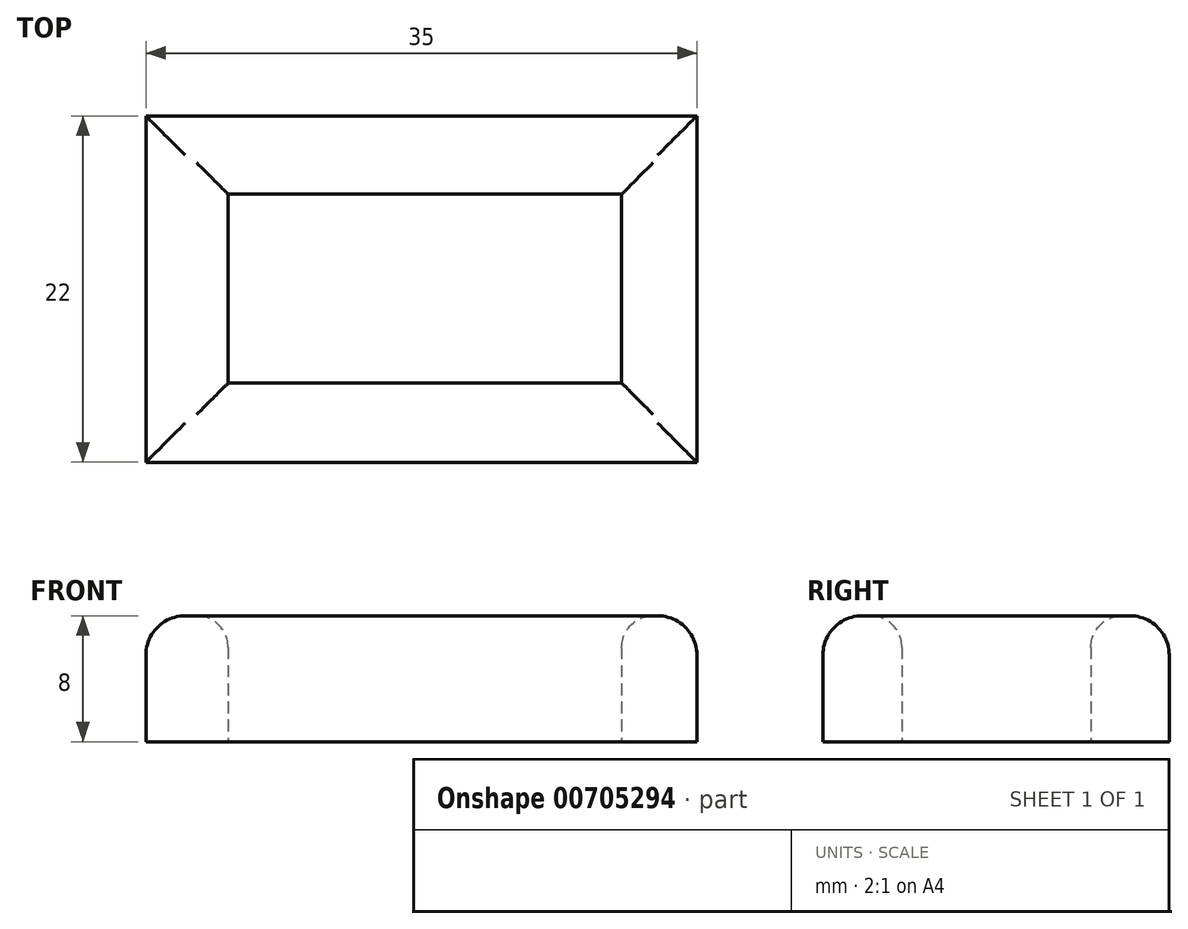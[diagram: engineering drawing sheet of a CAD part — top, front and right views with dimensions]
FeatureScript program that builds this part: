
annotation { "Feature Type Name" : "Feature", "Feature Type Description" : "" }
export const myFeature = defineFeature(function(context is Context, id is Id, definition is map)
    precondition{}
    {
        {
            var Q0;
            Q0=qCreatedBy(makeId("Top.planeOp"),FACE);
            var sketch = newSketch(context, id + "F0", { "sketchPlane" : qUnion([Q0])});
            skLineSegment(sketch, "E0.bottom", {"start": v(-54.07, 46.35) * mm, "end": v(-29.07, 46.35) * mm});
            skLineSegment(sketch, "E0.top", {"start": v(-54.07, 34.35) * mm, "end": v(-29.07, 34.35) * mm});
            skLineSegment(sketch, "E0.left", {"start": v(-54.07, 46.35) * mm, "end": v(-54.07, 34.35) * mm});
            skLineSegment(sketch, "E0.right", {"start": v(-29.07, 46.35) * mm, "end": v(-29.07, 34.35) * mm});
            skLineSegment(sketch, "E1.bottom", {"start": v(-59.3, 51.33) * mm, "end": v(-24.3, 51.33) * mm});
            skLineSegment(sketch, "E1.top", {"start": v(-59.3, 29.33) * mm, "end": v(-24.3, 29.33) * mm});
            skLineSegment(sketch, "E1.left", {"start": v(-59.3, 51.33) * mm, "end": v(-59.3, 29.33) * mm});
            skLineSegment(sketch, "E1.right", {"start": v(-24.3, 51.33) * mm, "end": v(-24.3, 29.33) * mm});
            skSolve(sketch);
        }
        {
            var Q0;
            Q0=makeQuery(id+"F0.imprint","IMPRINT",FACE,{"disambiguationData":[TD([[makeQuery(id+"F0.imprint","IMPRINT",EDGE,{"derivedFrom":sQuery(id+"F0.wireOp",EDGE,"E0.bottom")}),1.0]])]});
            extrude(context, id + "F1", {"entities" : qUnion([Q0]), "depth" : 8 * mm, "offsetDistance" : 25 * mm});
        }
        {
            var Q0;
            Q0=makeQuery(id+"F1.opExtrude","CAP_EDGE",EDGE,{"disambiguationData":[OSD([sQuery(id+"F0.wireOp",EDGE,"E1.top")])],"isStart":false});
            var Q1;
            Q1=makeQuery(id+"F1.opExtrude","CAP_EDGE",EDGE,{"disambiguationData":[OSD([sQuery(id+"F0.wireOp",EDGE,"E1.left")])],"isStart":false});
            var Q2;
            Q2=makeQuery(id+"F1.opExtrude","CAP_EDGE",EDGE,{"disambiguationData":[OSD([sQuery(id+"F0.wireOp",EDGE,"E1.bottom")])],"isStart":false});
            var Q3;
            Q3=makeQuery(id+"F1.opExtrude","CAP_EDGE",EDGE,{"disambiguationData":[OSD([sQuery(id+"F0.wireOp",EDGE,"E1.right")])],"isStart":false});
            fillet(context, id + "F2", {"entities" : qUnion([Q0, Q1, Q2, Q3]), "radius" : 2.5 * mm, "tangentPropagation" : true, "allowEdgeOverflow" : false});
        }
        {
            var Q0;
            Q0=makeQuery(id+"F1.opExtrude","CAP_EDGE",EDGE,{"disambiguationData":[OSD([sQuery(id+"F0.wireOp",EDGE,"E0.bottom")])],"isStart":false});
            var Q1;
            Q1=makeQuery(id+"F1.opExtrude","CAP_EDGE",EDGE,{"disambiguationData":[OSD([sQuery(id+"F0.wireOp",EDGE,"E0.left")])],"isStart":false});
            var Q2;
            Q2=makeQuery(id+"F1.opExtrude","CAP_EDGE",EDGE,{"disambiguationData":[OSD([sQuery(id+"F0.wireOp",EDGE,"E0.top")])],"isStart":false});
            var Q3;
            Q3=makeQuery(id+"F1.opExtrude","CAP_EDGE",EDGE,{"disambiguationData":[OSD([sQuery(id+"F0.wireOp",EDGE,"E0.right")])],"isStart":false});
            fillet(context, id + "F3", {"entities" : qUnion([Q0, Q1, Q2, Q3]), "radius" : 2 * mm, "tangentPropagation" : true, "allowEdgeOverflow" : false});
        }
    });
